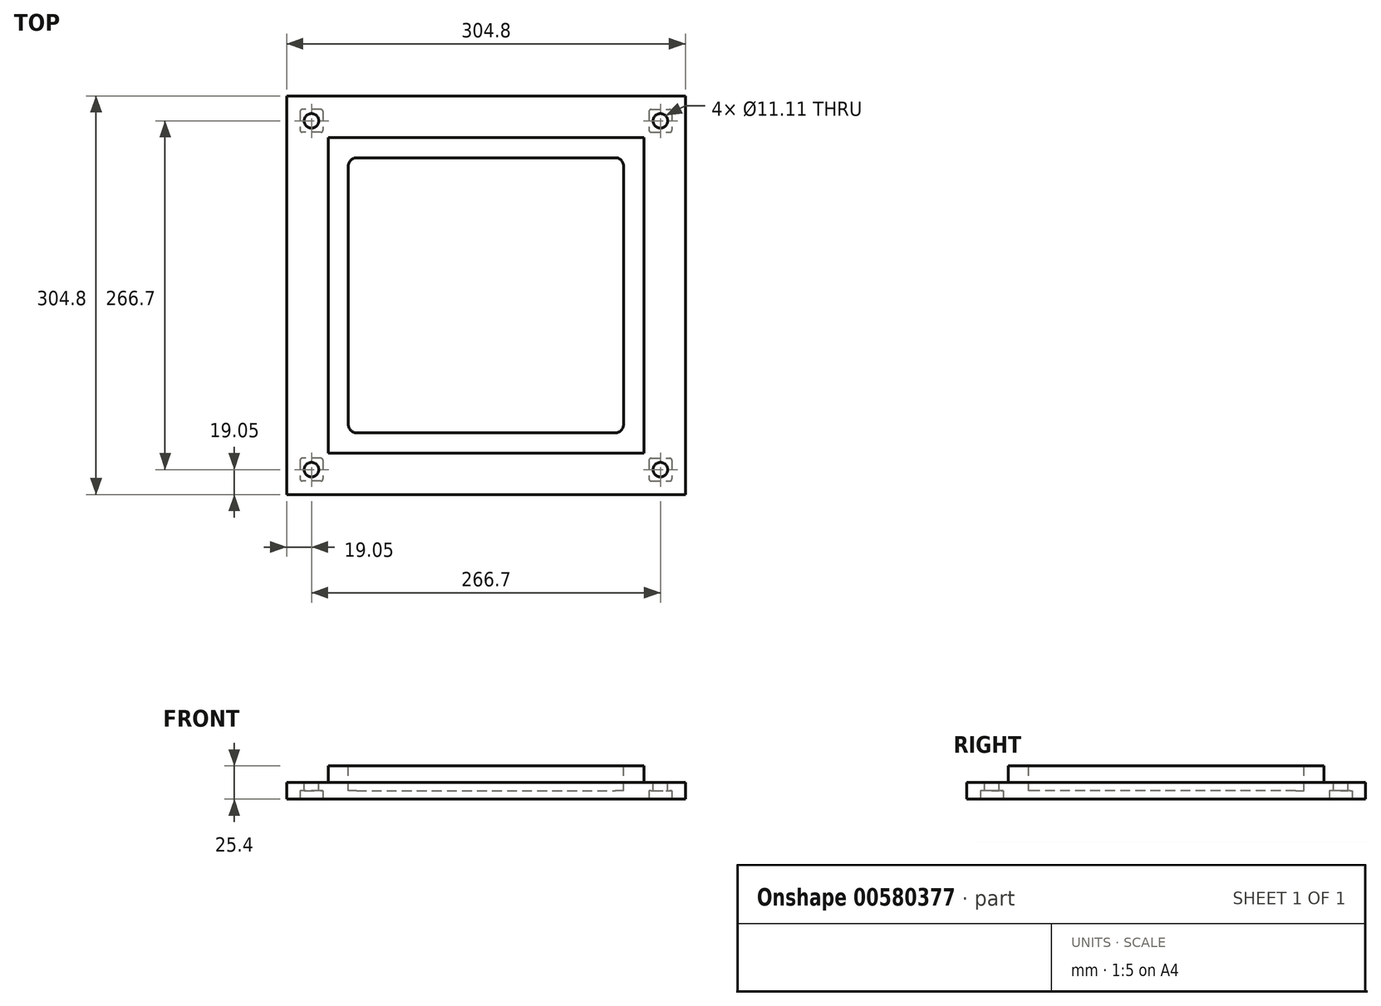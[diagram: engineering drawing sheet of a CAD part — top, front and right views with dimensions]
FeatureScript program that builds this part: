
annotation { "Feature Type Name" : "Feature", "Feature Type Description" : "" }
export const myFeature = defineFeature(function(context is Context, id is Id, definition is map)
    precondition{}
    {
        {
            var Q0;
            Q0=qCreatedBy(makeId("Top.planeOp"),FACE);
            var sketch = newSketch(context, id + "F0", { "sketchPlane" : qUnion([Q0])});
            skLineSegment(sketch, "E0.bottom", {"start": v(-152.4, 152.4) * mm, "end": v(152.4, 152.4) * mm});
            skLineSegment(sketch, "E0.top", {"start": v(-152.4, -152.4) * mm, "end": v(152.4, -152.4) * mm});
            skLineSegment(sketch, "E0.left", {"start": v(-152.4, 152.4) * mm, "end": v(-152.4, -152.4) * mm});
            skLineSegment(sketch, "E0.right", {"start": v(152.4, 152.4) * mm, "end": v(152.4, -152.4) * mm});
            skSolve(sketch);
        }
        {
            var Q0;
            Q0=qSketchRegion(id+"F0",true);
            extrude(context, id + "F1", {"entities" : qUnion([Q0]), "depth" : 25.4 * mm, "offsetDistance" : 25.4 * mm});
        }
        {
            var Q0;
            Q0=makeQuery(id+"F1.opExtrude","CAP_FACE",FACE,{"disambiguationData":[OSD([sQuery(id+"F0.wireOp",EDGE,"E0.bottom"),sQuery(id+"F0.wireOp",EDGE,"E0.top"),sQuery(id+"F0.wireOp",EDGE,"E0.left"),sQuery(id+"F0.wireOp",EDGE,"E0.right")])],"isStart":false});
            var sketch = newSketch(context, id + "F2", { "sketchPlane" : qUnion([Q0])});
            skLineSegment(sketch, "E1.bottom", {"start": v(-98.83, 105.18) * mm, "end": v(98.83, 105.18) * mm});
            skLineSegment(sketch, "E1.top", {"start": v(-98.83, -105.18) * mm, "end": v(98.83, -105.18) * mm});
            skLineSegment(sketch, "E1.left", {"start": v(-105.18, 98.83) * mm, "end": v(-105.18, -98.83) * mm});
            skLineSegment(sketch, "E1.right", {"start": v(105.18, 98.83) * mm, "end": v(105.18, -98.83) * mm});
            skPoint(sketch, "E2.visualSharp", {"position": v(-105.18, 105.18) * mm});
            skArc(sketch, "E2.filletArc", {"start": v(-98.83, 105.18) * mm, "mid": v(-103.32, 103.32) * mm, "end": v(-105.18, 98.83) * mm});
            skPoint(sketch, "E3.visualSharp", {"position": v(105.18, 105.18) * mm});
            skArc(sketch, "E3.filletArc", {"start": v(105.18, 98.83) * mm, "mid": v(103.32, 103.32) * mm, "end": v(98.83, 105.18) * mm});
            skPoint(sketch, "E4.visualSharp", {"position": v(105.18, -105.18) * mm});
            skArc(sketch, "E4.filletArc", {"start": v(98.83, -105.18) * mm, "mid": v(103.32, -103.32) * mm, "end": v(105.18, -98.83) * mm});
            skPoint(sketch, "E5.visualSharp", {"position": v(-105.18, -105.18) * mm});
            skArc(sketch, "E5.filletArc", {"start": v(-105.18, -98.83) * mm, "mid": v(-103.32, -103.32) * mm, "end": v(-98.83, -105.18) * mm});
            skSolve(sketch);
        }
        {
            var Q0;
            Q0=qSketchRegion(id+"F2",true);
            extrude(context, id + "F3", {"entities" : qUnion([Q0]), "operationType" : NewBodyOperationType.REMOVE, "oppositeDirection" : true, "depth" : 19.05 * mm, "offsetDistance" : 25.4 * mm});
        }
        {
            var Q0;
            Q0=makeQuery(id+"F1.opExtrude","CAP_FACE",FACE,{"disambiguationData":[OSD([sQuery(id+"F0.wireOp",EDGE,"E0.bottom"),sQuery(id+"F0.wireOp",EDGE,"E0.top"),sQuery(id+"F0.wireOp",EDGE,"E0.left"),sQuery(id+"F0.wireOp",EDGE,"E0.right")])],"isStart":false});
            var sketch = newSketch(context, id + "F4", { "sketchPlane" : qUnion([Q0])});
            skLineSegment(sketch, "E6.bottom", {"start": v(-152.4, 152.4) * mm, "end": v(152.4, 152.4) * mm});
            skLineSegment(sketch, "E6.top", {"start": v(-152.4, -152.4) * mm, "end": v(152.4, -152.4) * mm});
            skLineSegment(sketch, "E6.left", {"start": v(-152.4, 152.4) * mm, "end": v(-152.4, -152.4) * mm});
            skLineSegment(sketch, "E6.right", {"start": v(152.4, 152.4) * mm, "end": v(152.4, -152.4) * mm});
            skLineSegment(sketch, "E7.0", {"start": v(-120.65, 120.65) * mm, "end": v(120.65, 120.65) * mm});
            skLineSegment(sketch, "E7.1", {"start": v(-120.65, 120.65) * mm, "end": v(-120.65, -120.65) * mm});
            skLineSegment(sketch, "E7.2", {"start": v(-120.65, -120.65) * mm, "end": v(120.65, -120.65) * mm});
            skLineSegment(sketch, "E7.3", {"start": v(120.65, 120.65) * mm, "end": v(120.65, -120.65) * mm});
            skSolve(sketch);
        }
        {
            var Q0;
            Q0=qSketchRegion(id+"F4",true);
            extrude(context, id + "F5", {"entities" : qUnion([Q0]), "operationType" : NewBodyOperationType.REMOVE, "oppositeDirection" : true, "depth" : 12.7 * mm, "offsetDistance" : 25.4 * mm});
        }
        {
            var Q0;
            Q0=makeQuery(id+"F5.boolean.opBoolean","COPY",FACE,{"derivedFrom":makeQuery(id+"F5.opExtrude","CAP_FACE",FACE,{"disambiguationData":[OSD([sQuery(id+"F4.wireOp",EDGE,"E6.bottom"),sQuery(id+"F4.wireOp",EDGE,"E6.top"),sQuery(id+"F4.wireOp",EDGE,"E6.left"),sQuery(id+"F4.wireOp",EDGE,"E6.right"),sQuery(id+"F4.wireOp",EDGE,"E7.0"),sQuery(id+"F4.wireOp",EDGE,"E7.1"),sQuery(id+"F4.wireOp",EDGE,"E7.2"),sQuery(id+"F4.wireOp",EDGE,"E7.3")])],"isStart":false})});
            var sketch = newSketch(context, id + "F6", { "sketchPlane" : qUnion([Q0])});
            skPoint(sketch, "E8", {"position": v(-133.35, 133.35) * mm});
            skPoint(sketch, "E9", {"position": v(133.35, 133.35) * mm});
            skPoint(sketch, "E10", {"position": v(133.35, -133.35) * mm});
            skPoint(sketch, "E11", {"position": v(-133.35, -133.35) * mm});
            skSolve(sketch);
        }
        {
            var Q0;
            Q0=sQuery(id+"F6.wireOp",VERTEX,"E8");
            var Q1;
            Q1=sQuery(id+"F6.wireOp",VERTEX,"E9");
            var Q2;
            Q2=sQuery(id+"F6.wireOp",VERTEX,"E10");
            var Q3;
            Q3=sQuery(id+"F6.wireOp",VERTEX,"E11");
            var Q4;
            Q4=makeQuery(id+"F1.opExtrude","SWEPT_BODY",BODY,{"disambiguationData":[OSD([sQuery(id+"F0.wireOp",EDGE,"E0.bottom"),sQuery(id+"F0.wireOp",EDGE,"E0.top"),sQuery(id+"F0.wireOp",EDGE,"E0.left"),sQuery(id+"F0.wireOp",EDGE,"E0.right")])]});
            hole(context, id + "F7", {"style" : HoleStyle.SIMPLE, "endStyle" : HoleEndStyle.THROUGH, "holeDiameter" : 11.1 * mm, "majorDiameter" : 6.35 * mm, "isTappedThrough" : true, "tappedDepth" : 12.7 * mm, "tapClearance" : 3, "locations" : qUnion([Q0, Q1, Q2, Q3]), "scope" : qUnion([Q4])});
        }
        {
            var Q0;
            Q0=makeQuery(id+"F1.opExtrude","CAP_FACE",FACE,{"disambiguationData":[OSD([sQuery(id+"F0.wireOp",EDGE,"E0.bottom"),sQuery(id+"F0.wireOp",EDGE,"E0.top"),sQuery(id+"F0.wireOp",EDGE,"E0.left"),sQuery(id+"F0.wireOp",EDGE,"E0.right")])],"isStart":true});
            var sketch = newSketch(context, id + "F8", { "sketchPlane" : qUnion([Q0])});
            skLineSegment(sketch, "E12.bottom", {"start": v(-126.2, 124.62) * mm, "end": v(-140.5, 124.62) * mm});
            skLineSegment(sketch, "E12.top", {"start": v(-126.2, 142.08) * mm, "end": v(-140.5, 142.08) * mm});
            skLineSegment(sketch, "E12.left", {"start": v(-124.62, 126.2) * mm, "end": v(-124.62, 140.5) * mm});
            skLineSegment(sketch, "E12.right", {"start": v(-142.08, 126.2) * mm, "end": v(-142.08, 140.5) * mm});
            skPoint(sketch, "E12.middle", {"position": v(-133.35, 133.35) * mm});
            skLineSegment(sketch, "E13.bottom", {"start": v(126.2, 124.62) * mm, "end": v(140.5, 124.62) * mm});
            skLineSegment(sketch, "E13.top", {"start": v(126.2, 142.08) * mm, "end": v(140.5, 142.08) * mm});
            skLineSegment(sketch, "E13.left", {"start": v(124.62, 126.2) * mm, "end": v(124.62, 140.5) * mm});
            skLineSegment(sketch, "E13.right", {"start": v(142.08, 126.2) * mm, "end": v(142.08, 140.5) * mm});
            skPoint(sketch, "E13.middle", {"position": v(133.35, 133.35) * mm});
            skLineSegment(sketch, "E14.bottom", {"start": v(126.2, -142.08) * mm, "end": v(140.5, -142.08) * mm});
            skLineSegment(sketch, "E14.top", {"start": v(126.2, -124.62) * mm, "end": v(140.5, -124.62) * mm});
            skLineSegment(sketch, "E14.left", {"start": v(124.62, -140.5) * mm, "end": v(124.62, -126.2) * mm});
            skLineSegment(sketch, "E14.right", {"start": v(142.08, -140.5) * mm, "end": v(142.08, -126.2) * mm});
            skPoint(sketch, "E14.middle", {"position": v(133.35, -133.35) * mm});
            skLineSegment(sketch, "E15.bottom", {"start": v(-126.2, -142.08) * mm, "end": v(-140.5, -142.08) * mm});
            skLineSegment(sketch, "E15.top", {"start": v(-126.2, -124.62) * mm, "end": v(-140.5, -124.62) * mm});
            skLineSegment(sketch, "E15.left", {"start": v(-124.62, -140.5) * mm, "end": v(-124.62, -126.2) * mm});
            skLineSegment(sketch, "E15.right", {"start": v(-142.08, -140.5) * mm, "end": v(-142.08, -126.2) * mm});
            skPoint(sketch, "E15.middle", {"position": v(-133.35, -133.35) * mm});
            skPoint(sketch, "E16.visualSharp", {"position": v(-124.62, 142.08) * mm});
            skArc(sketch, "E16.filletArc", {"start": v(-124.62, 140.5) * mm, "mid": v(-125.08, 141.62) * mm, "end": v(-126.2, 142.08) * mm});
            skPoint(sketch, "E17.visualSharp", {"position": v(-124.62, 124.62) * mm});
            skArc(sketch, "E17.filletArc", {"start": v(-126.2, 124.62) * mm, "mid": v(-125.08, 125.08) * mm, "end": v(-124.62, 126.2) * mm});
            skPoint(sketch, "E18.visualSharp", {"position": v(-142.08, 124.62) * mm});
            skArc(sketch, "E18.filletArc", {"start": v(-142.08, 126.2) * mm, "mid": v(-141.62, 125.08) * mm, "end": v(-140.5, 124.62) * mm});
            skPoint(sketch, "E19.visualSharp", {"position": v(-142.08, 142.08) * mm});
            skArc(sketch, "E19.filletArc", {"start": v(-140.5, 142.08) * mm, "mid": v(-141.62, 141.62) * mm, "end": v(-142.08, 140.5) * mm});
            skPoint(sketch, "E20.visualSharp", {"position": v(124.62, 142.08) * mm});
            skArc(sketch, "E20.filletArc", {"start": v(126.2, 142.08) * mm, "mid": v(125.08, 141.62) * mm, "end": v(124.62, 140.5) * mm});
            skPoint(sketch, "E21.visualSharp", {"position": v(142.08, 142.08) * mm});
            skArc(sketch, "E21.filletArc", {"start": v(142.08, 140.5) * mm, "mid": v(141.62, 141.62) * mm, "end": v(140.5, 142.08) * mm});
            skPoint(sketch, "E22.visualSharp", {"position": v(142.08, 124.62) * mm});
            skArc(sketch, "E22.filletArc", {"start": v(140.5, 124.62) * mm, "mid": v(141.62, 125.08) * mm, "end": v(142.08, 126.2) * mm});
            skPoint(sketch, "E23.visualSharp", {"position": v(124.62, 124.62) * mm});
            skArc(sketch, "E23.filletArc", {"start": v(124.62, 126.2) * mm, "mid": v(125.08, 125.08) * mm, "end": v(126.2, 124.62) * mm});
            skPoint(sketch, "E24.visualSharp", {"position": v(124.62, -124.62) * mm});
            skArc(sketch, "E24.filletArc", {"start": v(126.2, -124.62) * mm, "mid": v(125.08, -125.08) * mm, "end": v(124.62, -126.2) * mm});
            skPoint(sketch, "E25.visualSharp", {"position": v(124.62, -142.08) * mm});
            skArc(sketch, "E25.filletArc", {"start": v(124.62, -140.5) * mm, "mid": v(125.08, -141.62) * mm, "end": v(126.2, -142.08) * mm});
            skPoint(sketch, "E26.visualSharp", {"position": v(142.08, -142.08) * mm});
            skArc(sketch, "E26.filletArc", {"start": v(140.5, -142.08) * mm, "mid": v(141.62, -141.62) * mm, "end": v(142.08, -140.5) * mm});
            skPoint(sketch, "E27.visualSharp", {"position": v(142.08, -124.62) * mm});
            skArc(sketch, "E27.filletArc", {"start": v(142.08, -126.2) * mm, "mid": v(141.62, -125.08) * mm, "end": v(140.5, -124.62) * mm});
            skPoint(sketch, "E28.visualSharp", {"position": v(-124.62, -124.62) * mm});
            skArc(sketch, "E28.filletArc", {"start": v(-124.62, -126.2) * mm, "mid": v(-125.08, -125.08) * mm, "end": v(-126.2, -124.62) * mm});
            skPoint(sketch, "E29.visualSharp", {"position": v(-124.62, -142.08) * mm});
            skArc(sketch, "E29.filletArc", {"start": v(-126.2, -142.08) * mm, "mid": v(-125.08, -141.62) * mm, "end": v(-124.62, -140.5) * mm});
            skPoint(sketch, "E30.visualSharp", {"position": v(-142.08, -142.08) * mm});
            skArc(sketch, "E30.filletArc", {"start": v(-142.08, -140.5) * mm, "mid": v(-141.62, -141.62) * mm, "end": v(-140.5, -142.08) * mm});
            skPoint(sketch, "E31.visualSharp", {"position": v(-142.08, -124.62) * mm});
            skArc(sketch, "E31.filletArc", {"start": v(-140.5, -124.62) * mm, "mid": v(-141.62, -125.08) * mm, "end": v(-142.08, -126.2) * mm});
            skSolve(sketch);
        }
        {
            var Q0;
            Q0=qSketchRegion(id+"F8",true);
            extrude(context, id + "F9", {"entities" : qUnion([Q0]), "operationType" : NewBodyOperationType.REMOVE, "oppositeDirection" : true, "depth" : 6.35 * mm, "offsetDistance" : 25.4 * mm});
        }
    });
